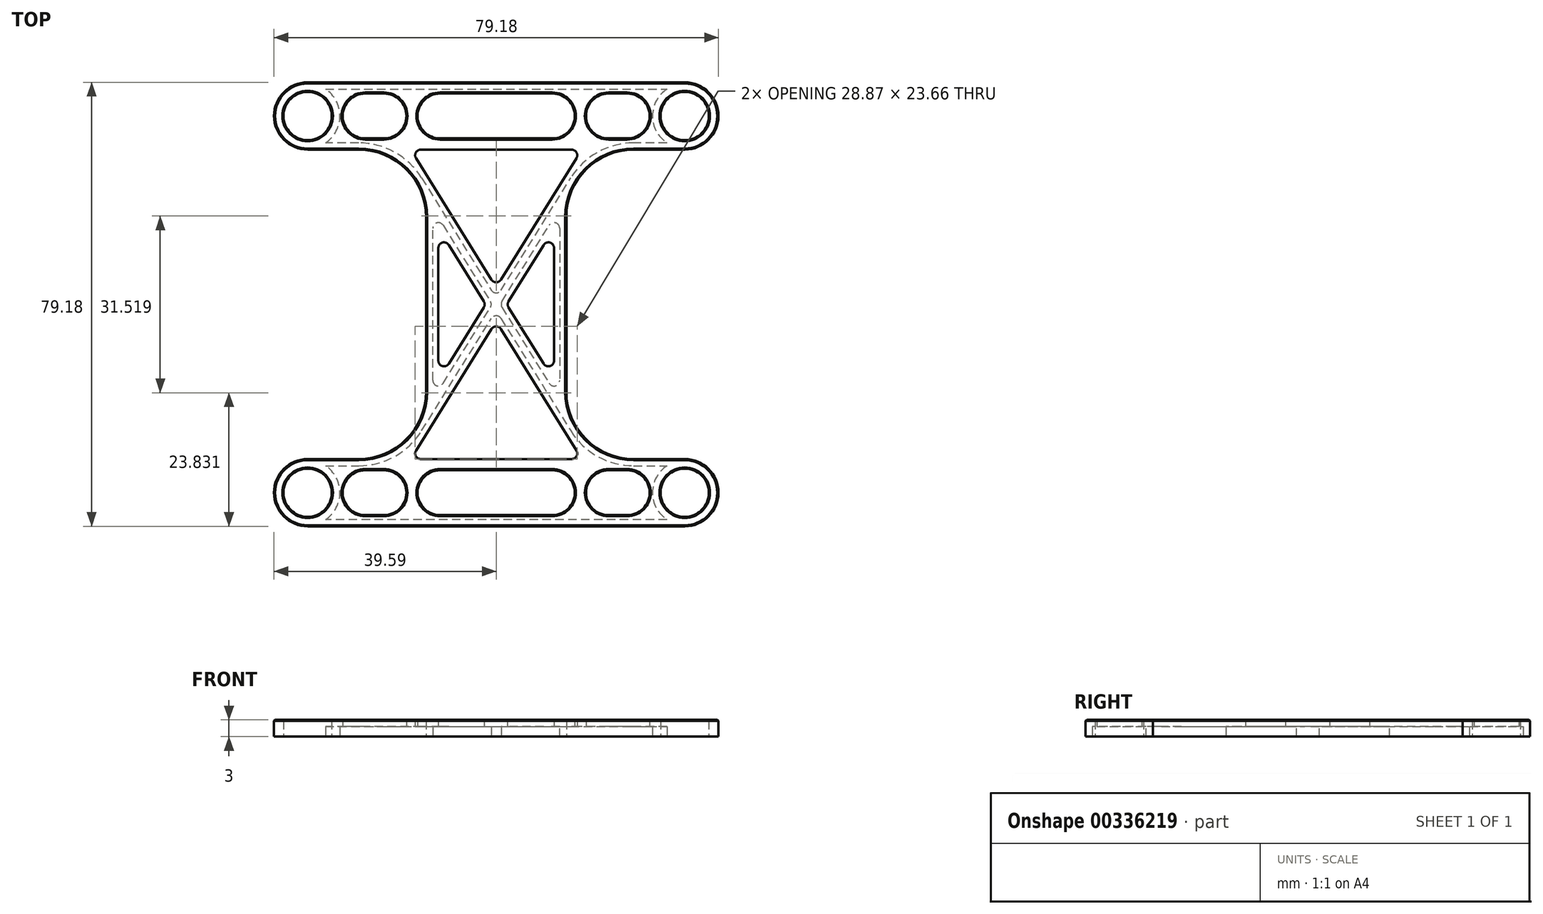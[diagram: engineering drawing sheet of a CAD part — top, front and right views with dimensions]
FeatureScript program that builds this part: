
annotation { "Feature Type Name" : "Feature", "Feature Type Description" : "" }
export const myFeature = defineFeature(function(context is Context, id is Id, definition is map)
    precondition{}
    {
        {
            var Q0;
            Q0=qCreatedBy(makeId("Top.planeOp"),FACE);
            var sketch = newSketch(context, id + "F0", { "sketchPlane" : qUnion([Q0])});
            skLineSegment(sketch, "E0.bottom", {"start": v(33.59, 33.59) * mm, "end": v(-33.59, 33.59) * mm, "construction": true});
            skLineSegment(sketch, "E0.top", {"start": v(33.59, -33.59) * mm, "end": v(-33.59, -33.59) * mm, "construction": true});
            skLineSegment(sketch, "E0.left", {"start": v(33.59, 33.59) * mm, "end": v(33.59, -33.59) * mm, "construction": true});
            skLineSegment(sketch, "E0.right", {"start": v(-33.59, 33.59) * mm, "end": v(-33.59, -33.59) * mm, "construction": true});
            skPoint(sketch, "E0.middle", {"position": v(0, 0) * mm});
            skCircle(sketch, "E1", {"center": v(33.59, 33.59) * mm, "radius": 4.25 * mm, "construction": true});
            skCircle(sketch, "E2", {"center": v(-33.59, 33.59) * mm, "radius": 4.25 * mm, "construction": true});
            skCircle(sketch, "E3", {"center": v(-33.59, -33.59) * mm, "radius": 4.25 * mm, "construction": true});
            skCircle(sketch, "E4", {"center": v(33.59, -33.59) * mm, "radius": 4.25 * mm, "construction": true});
            skLineSegment(sketch, "E5.bottom", {"start": v(10, 16.5) * mm, "end": v(-10, 16.5) * mm, "construction": true});
            skLineSegment(sketch, "E5.top", {"start": v(10, -16.5) * mm, "end": v(-10, -16.5) * mm, "construction": true});
            skLineSegment(sketch, "E5.left", {"start": v(10, 16.5) * mm, "end": v(10, -16.5) * mm, "construction": true});
            skLineSegment(sketch, "E5.right", {"start": v(-10, 16.5) * mm, "end": v(-10, -16.5) * mm, "construction": true});
            skLineSegment(sketch, "E6", {"start": v(33.59, 33.59) * mm, "end": v(-33.59, -33.59) * mm, "construction": true});
            skSolve(sketch);
        }
        {
            var Q0;
            Q0=qCreatedBy(makeId("Top.planeOp"),FACE);
            var sketch = newSketch(context, id + "F1", { "sketchPlane" : qUnion([Q0])});
            skCircle(sketch, "E7.0", {"center": v(33.59, 33.59) * mm, "radius": 4.25 * mm, "construction": true});
            skCircle(sketch, "E8.0", {"center": v(-33.59, 33.59) * mm, "radius": 4.25 * mm, "construction": true});
            skCircle(sketch, "E9.0", {"center": v(-33.59, -33.59) * mm, "radius": 4.25 * mm, "construction": true});
            skCircle(sketch, "E10.0", {"center": v(33.59, -33.59) * mm, "radius": 4.25 * mm, "construction": true});
            skLineSegment(sketch, "E11.0", {"start": v(33.59, 33.59) * mm, "end": v(33.59, -33.59) * mm, "construction": true});
            skLineSegment(sketch, "E12.0", {"start": v(33.59, 33.59) * mm, "end": v(-33.59, 33.59) * mm, "construction": true});
            skLineSegment(sketch, "E13.0", {"start": v(-33.59, 33.59) * mm, "end": v(-33.59, -33.59) * mm, "construction": true});
            skLineSegment(sketch, "E14.0", {"start": v(33.59, -33.59) * mm, "end": v(-33.59, -33.59) * mm, "construction": true});
            skArc(sketch, "E15.0.startCap", {"start": v(33.59, 39.59) * mm, "mid": v(39.59, 33.59) * mm, "end": v(33.59, 27.59) * mm});
            skArc(sketch, "E15.0.endCap", {"start": v(-33.59, 27.59) * mm, "mid": v(-39.59, 33.59) * mm, "end": v(-33.59, 39.59) * mm});
            skLineSegment(sketch, "E15.0.left", {"start": v(33.59, 27.59) * mm, "end": v(24.5, 27.59) * mm});
            skLineSegment(sketch, "E15.0.right", {"start": v(33.59, 39.59) * mm, "end": v(-33.59, 39.59) * mm});
            skArc(sketch, "E16.0.startCap", {"start": v(33.59, -27.59) * mm, "mid": v(39.59, -33.59) * mm, "end": v(33.59, -39.59) * mm});
            skArc(sketch, "E16.0.endCap", {"start": v(-33.59, -39.59) * mm, "mid": v(-39.59, -33.59) * mm, "end": v(-33.59, -27.59) * mm});
            skLineSegment(sketch, "E16.0.left", {"start": v(33.59, -39.59) * mm, "end": v(-33.59, -39.59) * mm});
            skLineSegment(sketch, "E16.0.right", {"start": v(33.59, -27.59) * mm, "end": v(24.5, -27.59) * mm});
            skLineSegment(sketch, "E17", {"start": v(-12.5, 15.59) * mm, "end": v(-12.5, -15.59) * mm});
            skLineSegment(sketch, "E18", {"start": v(12.5, 15.59) * mm, "end": v(12.5, -15.59) * mm});
            skLineSegment(sketch, "E19.trimOffspring", {"start": v(-24.5, 27.59) * mm, "end": v(-33.59, 27.59) * mm});
            skLineSegment(sketch, "E20.trimOffspring", {"start": v(-24.5, -27.59) * mm, "end": v(-33.59, -27.59) * mm});
            skPoint(sketch, "E21.visualSharp", {"position": v(12.5, 27.59) * mm});
            skArc(sketch, "E21.filletArc", {"start": v(24.5, 27.59) * mm, "mid": v(16.01, 24.07) * mm, "end": v(12.5, 15.59) * mm});
            skPoint(sketch, "E22.visualSharp", {"position": v(-12.5, 27.59) * mm});
            skArc(sketch, "E22.filletArc", {"start": v(-12.5, 15.59) * mm, "mid": v(-16.01, 24.07) * mm, "end": v(-24.5, 27.59) * mm});
            skPoint(sketch, "E23.visualSharp", {"position": v(-12.5, -27.59) * mm});
            skArc(sketch, "E23.filletArc", {"start": v(-24.5, -27.59) * mm, "mid": v(-16.01, -24.07) * mm, "end": v(-12.5, -15.59) * mm});
            skPoint(sketch, "E24.visualSharp", {"position": v(12.5, -27.59) * mm});
            skArc(sketch, "E24.filletArc", {"start": v(12.5, -15.59) * mm, "mid": v(16.01, -24.07) * mm, "end": v(24.5, -27.59) * mm});
            skSolve(sketch);
        }
        {
            var Q0;
            Q0=qCreatedBy(makeId("Top.planeOp"),FACE);
            var sketch = newSketch(context, id + "F2", { "sketchPlane" : qUnion([Q0])});
            skCircle(sketch, "E25.0", {"center": v(-33.59, 33.59) * mm, "radius": 4.25 * mm, "construction": true});
            skCircle(sketch, "E26.0", {"center": v(33.59, 33.59) * mm, "radius": 4.25 * mm, "construction": true});
            skCircle(sketch, "E27.0", {"center": v(-33.59, -33.59) * mm, "radius": 4.25 * mm, "construction": true});
            skCircle(sketch, "E28.0", {"center": v(33.59, -33.59) * mm, "radius": 4.25 * mm, "construction": true});
            skCircle(sketch, "E29.0", {"center": v(33.59, 33.59) * mm, "radius": 4.3 * mm});
            skCircle(sketch, "E30.0", {"center": v(-33.59, -33.59) * mm, "radius": 4.3 * mm});
            skCircle(sketch, "E31.0", {"center": v(33.59, -33.59) * mm, "radius": 4.3 * mm});
            skLineSegment(sketch, "E32", {"start": v(-23.34, 33.59) * mm, "end": v(-20, 33.59) * mm});
            skLineSegment(sketch, "E33", {"start": v(-10, 33.59) * mm, "end": v(10, 33.59) * mm});
            skArc(sketch, "E34.0.startCap", {"start": v(-23.34, 29.59) * mm, "mid": v(-27.34, 33.59) * mm, "end": v(-23.34, 37.59) * mm});
            skArc(sketch, "E34.0.endCap", {"start": v(-20, 37.59) * mm, "mid": v(-16, 33.59) * mm, "end": v(-20, 29.59) * mm});
            skLineSegment(sketch, "E34.0.left", {"start": v(-23.34, 37.59) * mm, "end": v(-20, 37.59) * mm});
            skLineSegment(sketch, "E34.0.right", {"start": v(-23.34, 29.59) * mm, "end": v(-20, 29.59) * mm});
            skArc(sketch, "E35.0.startCap", {"start": v(-10, 29.59) * mm, "mid": v(-14, 33.59) * mm, "end": v(-10, 37.59) * mm});
            skArc(sketch, "E35.0.endCap", {"start": v(10, 37.59) * mm, "mid": v(14, 33.59) * mm, "end": v(10, 29.59) * mm});
            skLineSegment(sketch, "E35.0.left", {"start": v(-10, 37.59) * mm, "end": v(10, 37.59) * mm});
            skLineSegment(sketch, "E35.0.right", {"start": v(-10, 29.59) * mm, "end": v(10, 29.59) * mm});
            skLineSegment(sketch, "E36", {"start": v(-16, 33.59) * mm, "end": v(-14, 33.59) * mm, "construction": true});
            skCircle(sketch, "E37.0", {"center": v(-33.59, 33.59) * mm, "radius": 4.3 * mm});
            skLineSegment(sketch, "E38", {"start": v(-27.34, 33.59) * mm, "end": v(-29.34, 33.59) * mm, "construction": true});
            skArc(sketch, "E39.MirrorCS", {"start": v(23.34, 29.59) * mm, "mid": v(27.34, 33.59) * mm, "end": v(23.34, 37.59) * mm});
            skLineSegment(sketch, "E40.MirrorCS", {"start": v(23.34, 37.59) * mm, "end": v(20, 37.59) * mm});
            skArc(sketch, "E41.MirrorCS", {"start": v(20, 37.59) * mm, "mid": v(16, 33.59) * mm, "end": v(20, 29.59) * mm});
            skLineSegment(sketch, "E42.MirrorCS", {"start": v(23.34, 29.59) * mm, "end": v(20, 29.59) * mm});
            skArc(sketch, "E43.MirrorCS", {"start": v(-23.34, -29.59) * mm, "mid": v(-27.34, -33.59) * mm, "end": v(-23.34, -37.59) * mm});
            skLineSegment(sketch, "E44.MirrorCS", {"start": v(-23.34, -37.59) * mm, "end": v(-20, -37.59) * mm});
            skLineSegment(sketch, "E45.MirrorCS", {"start": v(-23.34, -29.59) * mm, "end": v(-20, -29.59) * mm});
            skArc(sketch, "E46.MirrorCS", {"start": v(-20, -37.59) * mm, "mid": v(-16, -33.59) * mm, "end": v(-20, -29.59) * mm});
            skArc(sketch, "E47.MirrorCS", {"start": v(-10, -29.59) * mm, "mid": v(-14, -33.59) * mm, "end": v(-10, -37.59) * mm});
            skLineSegment(sketch, "E48.MirrorCS", {"start": v(-10, -29.59) * mm, "end": v(10, -29.59) * mm});
            skLineSegment(sketch, "E49.MirrorCS", {"start": v(-10, -37.59) * mm, "end": v(10, -37.59) * mm});
            skArc(sketch, "E50.MirrorCS", {"start": v(10, -37.59) * mm, "mid": v(14, -33.59) * mm, "end": v(10, -29.59) * mm});
            skArc(sketch, "E51.MirrorCS", {"start": v(20, -37.59) * mm, "mid": v(16, -33.59) * mm, "end": v(20, -29.59) * mm});
            skLineSegment(sketch, "E52.MirrorCS", {"start": v(23.34, -37.59) * mm, "end": v(20, -37.59) * mm});
            skLineSegment(sketch, "E53.MirrorCS", {"start": v(23.34, -29.59) * mm, "end": v(20, -29.59) * mm});
            skArc(sketch, "E54.MirrorCS", {"start": v(23.34, -29.59) * mm, "mid": v(27.34, -33.59) * mm, "end": v(23.34, -37.59) * mm});
            skSolve(sketch);
        }
        {
            var Q0;
            Q0=qCreatedBy(makeId("Top.planeOp"),FACE);
            var sketch = newSketch(context, id + "F3", { "sketchPlane" : qUnion([Q0])});
            skPoint(sketch, "E55.0", {"position": v(-33.59, 33.59) * mm});
            skPoint(sketch, "E56.0", {"position": v(33.59, 33.59) * mm});
            skPoint(sketch, "E57.0", {"position": v(33.59, -33.59) * mm});
            skPoint(sketch, "E58.0", {"position": v(-33.59, -33.59) * mm});
            skCircle(sketch, "E59.0", {"center": v(-33.59, 33.59) * mm, "radius": 4.25 * mm, "construction": true});
            skCircle(sketch, "E60.0", {"center": v(33.59, 33.59) * mm, "radius": 4.25 * mm, "construction": true});
            skCircle(sketch, "E61.0", {"center": v(33.59, -33.59) * mm, "radius": 4.25 * mm, "construction": true});
            skCircle(sketch, "E62.0", {"center": v(-33.59, -33.59) * mm, "radius": 4.25 * mm, "construction": true});
            skCircle(sketch, "E63.0", {"center": v(33.59, 33.59) * mm, "radius": 5.75 * mm});
            skCircle(sketch, "E64.0", {"center": v(-33.59, 33.59) * mm, "radius": 5.75 * mm});
            skCircle(sketch, "E65.0", {"center": v(33.59, -33.59) * mm, "radius": 5.75 * mm});
            skCircle(sketch, "E66.0", {"center": v(-33.59, -33.59) * mm, "radius": 5.75 * mm});
            skSolve(sketch);
        }
        {
            var Q0;
            Q0=qCreatedBy(makeId("Front.planeOp"),FACE);
            var sketch = newSketch(context, id + "F4", { "sketchPlane" : qUnion([Q0])});
            skLineSegment(sketch, "E67", {"start": v(0, 0) * mm, "end": v(0, -3) * mm});
            skLineSegment(sketch, "E68", {"start": v(0, -3) * mm, "end": v(0, -6) * mm});
            skSolve(sketch);
        }
        {
            var Q0;
            Q0=qSketchRegion(id+"F1",true);
            var Q1;
            Q1=sQuery(id+"F4.wireOp",EDGE,"E67");
            sweep(context, id + "F5", {"profiles" : qUnion([Q0]), "path" : qUnion([Q1])});
        }
        {
            var Q0;
            Q0=makeQuery(id+"F5.opSweep","CAP_FACE",FACE,{"disambiguationData":[OSD([sQuery(id+"F1.wireOp",EDGE,"E15.0.startCap"),sQuery(id+"F1.wireOp",EDGE,"E15.0.endCap"),sQuery(id+"F1.wireOp",EDGE,"E15.0.left"),sQuery(id+"F1.wireOp",EDGE,"E15.0.right"),sQuery(id+"F1.wireOp",EDGE,"E16.0.startCap"),sQuery(id+"F1.wireOp",EDGE,"E16.0.endCap"),sQuery(id+"F1.wireOp",EDGE,"E16.0.left"),sQuery(id+"F1.wireOp",EDGE,"E16.0.right"),sQuery(id+"F1.wireOp",EDGE,"E17"),sQuery(id+"F1.wireOp",EDGE,"E18"),sQuery(id+"F1.wireOp",EDGE,"E19.trimOffspring"),sQuery(id+"F1.wireOp",EDGE,"E20.trimOffspring"),sQuery(id+"F1.wireOp",EDGE,"E21.filletArc"),sQuery(id+"F1.wireOp",EDGE,"E22.filletArc"),sQuery(id+"F1.wireOp",EDGE,"E23.filletArc"),sQuery(id+"F1.wireOp",EDGE,"E24.filletArc"),sQuery(id+"F4.wireOp",VERTEX,"E67.end")])],"isStart":false});
            shell(context, id + "F6", {"entities" : qUnion([Q0]), "thickness" : 1.2 * mm});
        }
        {
            var Q0;
            Q0=qSketchRegion(id+"F3",true);
            var Q1;
            Q1=sQuery(id+"F4.wireOp",EDGE,"E67");
            sweep(context, id + "F7", {"operationType" : NewBodyOperationType.ADD, "profiles" : qUnion([Q0]), "path" : qUnion([Q1])});
        }
        {
            var Q0;
            Q0=qSketchRegion(id+"F2",true);
            var Q1;
            Q1=sQuery(id+"F4.wireOp",EDGE,"E67");
            var Q2;
            Q2=sQuery(id+"F4.wireOp",EDGE,"E68");
            sweep(context, id + "F8", {"operationType" : NewBodyOperationType.REMOVE, "profiles" : qUnion([Q0]), "path" : qUnion([Q1, Q2])});
        }
        {
            var Q0;
            Q0=makeQuery(id+"F5.opSweep","CAP_FACE",FACE,{"disambiguationData":[OSD([sQuery(id+"F1.wireOp",EDGE,"E15.0.startCap"),sQuery(id+"F1.wireOp",EDGE,"E15.0.endCap"),sQuery(id+"F1.wireOp",EDGE,"E15.0.left"),sQuery(id+"F1.wireOp",EDGE,"E15.0.right"),sQuery(id+"F1.wireOp",EDGE,"E16.0.startCap"),sQuery(id+"F1.wireOp",EDGE,"E16.0.endCap"),sQuery(id+"F1.wireOp",EDGE,"E16.0.left"),sQuery(id+"F1.wireOp",EDGE,"E16.0.right"),sQuery(id+"F1.wireOp",EDGE,"E17"),sQuery(id+"F1.wireOp",EDGE,"E18"),sQuery(id+"F1.wireOp",EDGE,"E19.trimOffspring"),sQuery(id+"F1.wireOp",EDGE,"E20.trimOffspring"),sQuery(id+"F1.wireOp",EDGE,"E21.filletArc"),sQuery(id+"F1.wireOp",EDGE,"E22.filletArc"),sQuery(id+"F1.wireOp",EDGE,"E23.filletArc"),sQuery(id+"F1.wireOp",EDGE,"E24.filletArc"),sQuery(id+"F4.wireOp",VERTEX,"E67.start")])],"isStart":true});
            chamfer(context, id + "F9", {"entities" : qUnion([Q0]), "width" : 0.2 * mm});
        }
        {
            var Q0;
            {var subQ0=sQuery(id+"F4.wireOp",VERTEX,"E67.end");Q0=makeQuery(id+"F7.boolean.opBoolean","MERGE",FACE,{"derivedFrom":[makeQuery(id+"F5.opSweep","CAP_FACE",FACE,{"disambiguationData":[OSD([sQuery(id+"F1.wireOp",EDGE,"E15.0.startCap"),sQuery(id+"F1.wireOp",EDGE,"E15.0.endCap"),sQuery(id+"F1.wireOp",EDGE,"E15.0.left"),sQuery(id+"F1.wireOp",EDGE,"E15.0.right"),sQuery(id+"F1.wireOp",EDGE,"E16.0.startCap"),sQuery(id+"F1.wireOp",EDGE,"E16.0.endCap"),sQuery(id+"F1.wireOp",EDGE,"E16.0.left"),sQuery(id+"F1.wireOp",EDGE,"E16.0.right"),sQuery(id+"F1.wireOp",EDGE,"E17"),sQuery(id+"F1.wireOp",EDGE,"E18"),sQuery(id+"F1.wireOp",EDGE,"E19.trimOffspring"),sQuery(id+"F1.wireOp",EDGE,"E20.trimOffspring"),sQuery(id+"F1.wireOp",EDGE,"E21.filletArc"),sQuery(id+"F1.wireOp",EDGE,"E22.filletArc"),sQuery(id+"F1.wireOp",EDGE,"E23.filletArc"),sQuery(id+"F1.wireOp",EDGE,"E24.filletArc"),subQ0])],"isStart":false}),makeQuery(id+"F7.opSweep","CAP_FACE",FACE,{"disambiguationData":[OSD([sQuery(id+"F3.wireOp",EDGE,"E63.0"),subQ0])],"isStart":false}),makeQuery(id+"F7.opSweep","CAP_FACE",FACE,{"disambiguationData":[OSD([sQuery(id+"F3.wireOp",EDGE,"E64.0"),subQ0])],"isStart":false}),makeQuery(id+"F7.opSweep","CAP_FACE",FACE,{"disambiguationData":[OSD([sQuery(id+"F3.wireOp",EDGE,"E65.0"),subQ0])],"isStart":false}),makeQuery(id+"F7.opSweep","CAP_FACE",FACE,{"disambiguationData":[OSD([sQuery(id+"F3.wireOp",EDGE,"E66.0"),subQ0])],"isStart":false})]});}
            var sketch = newSketch(context, id + "F10", { "sketchPlane" : qUnion([Q0])});
            skLineSegment(sketch, "E69", {"start": v(-13.28, -22.55) * mm, "end": v(14.3, 21.91) * mm});
            skLineSegment(sketch, "E70", {"start": v(-13.28, 22.55) * mm, "end": v(14.3, -21.91) * mm});
            skLineSegment(sketch, "E71", {"start": v(-14.3, -21.91) * mm, "end": v(13.28, 22.55) * mm});
            skLineSegment(sketch, "E72", {"start": v(-14.3, 21.91) * mm, "end": v(13.28, -22.55) * mm});
            skLineSegment(sketch, "E73", {"start": v(-14.3, -21.91) * mm, "end": v(-13.28, -22.55) * mm});
            skLineSegment(sketch, "E74", {"start": v(13.28, -22.55) * mm, "end": v(14.3, -21.91) * mm});
            skLineSegment(sketch, "E75", {"start": v(13.28, 22.55) * mm, "end": v(14.3, 21.91) * mm});
            skLineSegment(sketch, "E76", {"start": v(-13.28, 22.55) * mm, "end": v(-14.3, 21.91) * mm});
            skSolve(sketch);
        }
        {
            var Q0;
            Q0 = qSketchRegion(id + "F10", true);
            var Q1;
            Q1=makeQuery(id+"F6.opShell","OFFSET_FACE",FACE,{"disambiguationData":[OSD([sQuery(id+"F1.wireOp",EDGE,"E15.0.startCap"),sQuery(id+"F1.wireOp",EDGE,"E15.0.endCap"),sQuery(id+"F1.wireOp",EDGE,"E15.0.left"),sQuery(id+"F1.wireOp",EDGE,"E15.0.right"),sQuery(id+"F1.wireOp",EDGE,"E16.0.startCap"),sQuery(id+"F1.wireOp",EDGE,"E16.0.endCap"),sQuery(id+"F1.wireOp",EDGE,"E16.0.left"),sQuery(id+"F1.wireOp",EDGE,"E16.0.right"),sQuery(id+"F1.wireOp",EDGE,"E17"),sQuery(id+"F1.wireOp",EDGE,"E18"),sQuery(id+"F1.wireOp",EDGE,"E19.trimOffspring"),sQuery(id+"F1.wireOp",EDGE,"E20.trimOffspring"),sQuery(id+"F1.wireOp",EDGE,"E21.filletArc"),sQuery(id+"F1.wireOp",EDGE,"E22.filletArc"),sQuery(id+"F1.wireOp",EDGE,"E23.filletArc"),sQuery(id+"F1.wireOp",EDGE,"E24.filletArc"),sQuery(id+"F4.wireOp",VERTEX,"E67.start")])]});
            extrude(context, id + "F11", {"entities" : qUnion([Q0]), "operationType" : NewBodyOperationType.ADD, "endBound" : BoundingType.UP_TO_SURFACE, "oppositeDirection" : true, "endBoundEntityFace" : qUnion([Q1]), "depth" : 25 * mm});
        }
        {
            var Q0;
            Q0=makeQuery(id+"F11.opExtrude","SWEPT_EDGE",EDGE,{"disambiguationData":[OSD([sQuery(id+"F10.wireOp",EDGE,"E69"),sQuery(id+"F10.wireOp",EDGE,"E72")])]});
            var Q1;
            Q1=makeQuery(id+"F11.opExtrude","SWEPT_EDGE",EDGE,{"disambiguationData":[OSD([sQuery(id+"F10.wireOp",EDGE,"E69"),sQuery(id+"F10.wireOp",EDGE,"E70")])]});
            var Q2;
            Q2=makeQuery(id+"F11.opExtrude","SWEPT_EDGE",EDGE,{"disambiguationData":[OSD([sQuery(id+"F10.wireOp",EDGE,"E71"),sQuery(id+"F10.wireOp",EDGE,"E72")])]});
            var Q3;
            Q3=makeQuery(id+"F11.opExtrude","SWEPT_EDGE",EDGE,{"disambiguationData":[OSD([sQuery(id+"F10.wireOp",EDGE,"E70"),sQuery(id+"F10.wireOp",EDGE,"E71")])]});
            var Q4;
            {var subQ0=sQuery(id+"F10.wireOp",EDGE,"E69");var subQ1=sQuery(id+"F4.wireOp",VERTEX,"E67.end");var subQ2=sQuery(id+"F1.wireOp",EDGE,"E24.filletArc");var subQ3=makeQuery(id+"F10.imprint","INTERSECT",VERTEX,{"derivedFrom":[makeQuery(id+"F6.opShell","OFFSET_EDGE",EDGE,{"disambiguationData":[OSD([subQ2,subQ1])]}),subQ0]});Q4=makeQuery(id+"F11.boolean.opBoolean","INTERSECT",EDGE,{"derivedFrom":[makeQuery(id+"F6.opShell","OFFSET_FACE",FACE,{"disambiguationData":[OSD([subQ2,sQuery(id+"F4.wireOp",EDGE,"E67")])]}),makeQuery(id+"F11.opExtrude","SWEPT_FACE",FACE,{"disambiguationData":[OSD([subQ0]),TDD([makeQuery(id+"F10.imprint","IMPRINT",EDGE,{"disambiguationData":[TD([[makeQuery(id+"F10.imprint","INTERSECT",VERTEX,{"derivedFrom":[subQ0,sQuery(id+"F10.wireOp",EDGE,"E70")]}),-1.0]])],"derivedFrom":subQ0}),makeQuery(id+"F10.imprint","IMPRINT",EDGE,{"disambiguationData":[TD([[subQ3,-1.0]])],"derivedFrom":subQ0})])]})]});}
            var Q5;
            {var subQ0=sQuery(id+"F10.wireOp",EDGE,"E72");var subQ1=sQuery(id+"F4.wireOp",VERTEX,"E67.end");var subQ2=sQuery(id+"F1.wireOp",EDGE,"E23.filletArc");var subQ3=makeQuery(id+"F10.imprint","INTERSECT",VERTEX,{"derivedFrom":[makeQuery(id+"F6.opShell","OFFSET_EDGE",EDGE,{"disambiguationData":[OSD([subQ2,subQ1])]}),subQ0]});Q5=makeQuery(id+"F11.boolean.opBoolean","INTERSECT",EDGE,{"derivedFrom":[makeQuery(id+"F6.opShell","OFFSET_FACE",FACE,{"disambiguationData":[OSD([subQ2,sQuery(id+"F4.wireOp",EDGE,"E67")])]}),makeQuery(id+"F11.opExtrude","SWEPT_FACE",FACE,{"disambiguationData":[OSD([subQ0]),TDD([makeQuery(id+"F10.imprint","IMPRINT",EDGE,{"disambiguationData":[TD([[subQ3,1.0]])],"derivedFrom":subQ0}),makeQuery(id+"F10.imprint","IMPRINT",EDGE,{"disambiguationData":[TD([[makeQuery(id+"F10.imprint","INTERSECT",VERTEX,{"derivedFrom":[sQuery(id+"F10.wireOp",EDGE,"E71"),subQ0]}),1.0]])],"derivedFrom":subQ0})])]})]});}
            var Q6;
            {var subQ0=sQuery(id+"F10.wireOp",EDGE,"E70");var subQ1=sQuery(id+"F4.wireOp",VERTEX,"E67.end");var subQ2=sQuery(id+"F1.wireOp",EDGE,"E21.filletArc");var subQ3=makeQuery(id+"F10.imprint","INTERSECT",VERTEX,{"derivedFrom":[makeQuery(id+"F6.opShell","OFFSET_EDGE",EDGE,{"disambiguationData":[OSD([subQ2,subQ1])]}),subQ0]});Q6=makeQuery(id+"F11.boolean.opBoolean","INTERSECT",EDGE,{"derivedFrom":[makeQuery(id+"F6.opShell","OFFSET_FACE",FACE,{"disambiguationData":[OSD([subQ2,sQuery(id+"F4.wireOp",EDGE,"E67")])]}),makeQuery(id+"F11.opExtrude","SWEPT_FACE",FACE,{"disambiguationData":[OSD([subQ0]),TDD([makeQuery(id+"F10.imprint","IMPRINT",EDGE,{"disambiguationData":[TD([[makeQuery(id+"F10.imprint","INTERSECT",VERTEX,{"derivedFrom":[sQuery(id+"F10.wireOp",EDGE,"E69"),subQ0]}),-1.0]])],"derivedFrom":subQ0}),makeQuery(id+"F10.imprint","IMPRINT",EDGE,{"disambiguationData":[TD([[subQ3,-1.0]])],"derivedFrom":subQ0})])]})]});}
            var Q7;
            {var subQ0=sQuery(id+"F10.wireOp",EDGE,"E71");var subQ1=sQuery(id+"F4.wireOp",VERTEX,"E67.end");var subQ2=sQuery(id+"F1.wireOp",EDGE,"E22.filletArc");var subQ3=makeQuery(id+"F10.imprint","INTERSECT",VERTEX,{"derivedFrom":[makeQuery(id+"F6.opShell","OFFSET_EDGE",EDGE,{"disambiguationData":[OSD([subQ2,subQ1])]}),subQ0]});Q7=makeQuery(id+"F11.boolean.opBoolean","INTERSECT",EDGE,{"derivedFrom":[makeQuery(id+"F6.opShell","OFFSET_FACE",FACE,{"disambiguationData":[OSD([subQ2,sQuery(id+"F4.wireOp",EDGE,"E67")])]}),makeQuery(id+"F11.opExtrude","SWEPT_FACE",FACE,{"disambiguationData":[OSD([subQ0]),TDD([makeQuery(id+"F10.imprint","IMPRINT",EDGE,{"disambiguationData":[TD([[subQ3,1.0]])],"derivedFrom":subQ0}),makeQuery(id+"F10.imprint","IMPRINT",EDGE,{"disambiguationData":[TD([[makeQuery(id+"F10.imprint","INTERSECT",VERTEX,{"derivedFrom":[subQ0,sQuery(id+"F10.wireOp",EDGE,"E72")]}),1.0]])],"derivedFrom":subQ0})])]})]});}
            fillet(context, id + "F12", {"entities" : qUnion([Q0, Q1, Q2, Q3, Q4, Q5, Q6, Q7]), "radius" : 1 * mm, "allowEdgeOverflow" : false});
        }
        {
            var Q0;
            {var subQ0=sQuery(id+"F4.wireOp",EDGE,"E67");var subQ1=sQuery(id+"F1.wireOp",EDGE,"E16.0.left");var subQ4=sQuery(id+"F1.wireOp",EDGE,"E23.filletArc");var subQ7=sQuery(id+"F1.wireOp",EDGE,"E24.filletArc");var subQ8=sQuery(id+"F1.wireOp",EDGE,"E16.0.right");var subQ9=sQuery(id+"F1.wireOp",EDGE,"E20.trimOffspring");Q0=makeQuery(id+"F11.boolean.opBoolean","SPLIT",FACE,{"disambiguationData":[TD([makeQuery(id+"F6.opShell","OFFSET_FACE",FACE,{"disambiguationData":[OSD([subQ1,subQ0])]})])],"derivedFrom":makeQuery(id+"F6.opShell","OFFSET_FACE",FACE,{"disambiguationData":[OSD([sQuery(id+"F1.wireOp",EDGE,"E15.0.startCap"),sQuery(id+"F1.wireOp",EDGE,"E15.0.endCap"),sQuery(id+"F1.wireOp",EDGE,"E15.0.left"),sQuery(id+"F1.wireOp",EDGE,"E15.0.right"),sQuery(id+"F1.wireOp",EDGE,"E16.0.startCap"),sQuery(id+"F1.wireOp",EDGE,"E16.0.endCap"),subQ1,subQ8,sQuery(id+"F1.wireOp",EDGE,"E17"),sQuery(id+"F1.wireOp",EDGE,"E18"),sQuery(id+"F1.wireOp",EDGE,"E19.trimOffspring"),subQ9,sQuery(id+"F1.wireOp",EDGE,"E21.filletArc"),sQuery(id+"F1.wireOp",EDGE,"E22.filletArc"),subQ4,subQ7,sQuery(id+"F4.wireOp",VERTEX,"E67.start")])]})});}
            var sketch = newSketch(context, id + "F13", { "sketchPlane" : qUnion([Q0])});
            skLineSegment(sketch, "E77", {"start": v(0, 29.59) * mm, "end": v(0, 28.59) * mm, "construction": true});
            skPoint(sketch, "E77.endSnap0", {"position": v(0, 29.59) * mm});
            skLineSegment(sketch, "E78.0.0", {"start": v(-13.28, 22.55) * mm, "end": v(-0.85, 2.5) * mm, "construction": true});
            skArc(sketch, "E78.0.1", {"start": v(-0.85, 2.5) * mm, "mid": v(0, 2.03) * mm, "end": v(0.85, 2.5) * mm, "construction": true});
            skLineSegment(sketch, "E78.0.2", {"start": v(0.85, 2.5) * mm, "end": v(13.28, 22.55) * mm, "construction": true});
            skArc(sketch, "E78.0.3", {"start": v(13.28, 22.55) * mm, "mid": v(17.1, 26.52) * mm, "end": v(22.21, 28.59) * mm, "construction": true});
            skLineSegment(sketch, "E78.0.4", {"start": v(24.5, 28.79) * mm, "end": v(30.42, 28.79) * mm, "construction": true});
            skArc(sketch, "E78.0.5", {"start": v(30.42, 28.79) * mm, "mid": v(27.84, 33.59) * mm, "end": v(30.42, 38.39) * mm, "construction": true});
            skLineSegment(sketch, "E78.0.6", {"start": v(30.42, 38.39) * mm, "end": v(-30.42, 38.39) * mm, "construction": true});
            skArc(sketch, "E78.0.7", {"start": v(-30.42, 38.39) * mm, "mid": v(-27.84, 33.59) * mm, "end": v(-30.42, 28.79) * mm, "construction": true});
            skLineSegment(sketch, "E78.0.8", {"start": v(-30.42, 28.79) * mm, "end": v(-24.5, 28.79) * mm, "construction": true});
            skArc(sketch, "E78.0.9", {"start": v(-24.5, 28.79) * mm, "mid": v(-23.35, 28.74) * mm, "end": v(-22.21, 28.59) * mm, "construction": true});
            skLineSegment(sketch, "E79", {"start": v(-26.79, 28.59) * mm, "end": v(26.79, 28.59) * mm, "construction": true});
            skArc(sketch, "E80", {"start": v(-22.21, 28.59) * mm, "mid": v(-17.1, 26.52) * mm, "end": v(-13.28, 22.55) * mm, "construction": true});
            skArc(sketch, "E81", {"start": v(22.21, 28.59) * mm, "mid": v(23.35, 28.74) * mm, "end": v(24.5, 28.79) * mm, "construction": true});
            skLineSegment(sketch, "E82.0", {"start": v(-15.23, 27.59) * mm, "end": v(0, 3.03) * mm});
            skLineSegment(sketch, "E82.1", {"start": v(-15.23, 27.59) * mm, "end": v(15.23, 27.59) * mm});
            skLineSegment(sketch, "E82.2", {"start": v(0, 3.03) * mm, "end": v(15.23, 27.59) * mm});
            skLineSegment(sketch, "E83.0", {"start": v(-1.88, 0) * mm, "end": v(-10.3, 13.57) * mm});
            skLineSegment(sketch, "E83.1", {"start": v(-10.3, -13.57) * mm, "end": v(-1.88, 0) * mm});
            skLineSegment(sketch, "E83.2", {"start": v(-10.3, 13.57) * mm, "end": v(-10.3, -13.57) * mm});
            skLineSegment(sketch, "E84.0", {"start": v(1.88, 0) * mm, "end": v(10.3, -13.57) * mm});
            skLineSegment(sketch, "E84.1", {"start": v(10.3, 13.57) * mm, "end": v(1.88, 0) * mm});
            skLineSegment(sketch, "E84.2", {"start": v(10.3, -13.57) * mm, "end": v(10.3, 13.57) * mm});
            skLineSegment(sketch, "E85.MirrorCS", {"start": v(-15.23, -27.59) * mm, "end": v(0, -3.03) * mm});
            skLineSegment(sketch, "E86.MirrorCS", {"start": v(0, -3.03) * mm, "end": v(15.23, -27.59) * mm});
            skLineSegment(sketch, "E87.MirrorCS", {"start": v(-15.23, -27.59) * mm, "end": v(15.23, -27.59) * mm});
            skSolve(sketch);
        }
        {
            var Q0;
            Q0 = qSketchRegion(id + "F13", true);
            extrude(context, id + "F14", {"entities" : qUnion([Q0]), "operationType" : NewBodyOperationType.REMOVE, "endBound" : BoundingType.THROUGH_ALL, "oppositeDirection" : true, "depth" : 25 * mm});
        }
        {
            var Q0;
            Q0=makeQuery(id+"F14.boolean.opBoolean","COPY",EDGE,{"derivedFrom":makeQuery(id+"F14.opExtrude","SWEPT_EDGE",EDGE,{"disambiguationData":[OSD([sQuery(id+"F13.wireOp",EDGE,"E82.0"),sQuery(id+"F13.wireOp",EDGE,"E82.1")])]})});
            var Q1;
            Q1=makeQuery(id+"F14.boolean.opBoolean","COPY",EDGE,{"derivedFrom":makeQuery(id+"F14.opExtrude","SWEPT_EDGE",EDGE,{"disambiguationData":[OSD([sQuery(id+"F13.wireOp",EDGE,"E82.1"),sQuery(id+"F13.wireOp",EDGE,"E82.2")])]})});
            var Q2;
            Q2=makeQuery(id+"F14.boolean.opBoolean","COPY",EDGE,{"derivedFrom":makeQuery(id+"F14.opExtrude","SWEPT_EDGE",EDGE,{"disambiguationData":[OSD([sQuery(id+"F13.wireOp",EDGE,"E82.0"),sQuery(id+"F13.wireOp",EDGE,"E82.2")])]})});
            var Q3;
            Q3=makeQuery(id+"F14.boolean.opBoolean","COPY",EDGE,{"derivedFrom":makeQuery(id+"F14.opExtrude","SWEPT_EDGE",EDGE,{"disambiguationData":[OSD([sQuery(id+"F13.wireOp",EDGE,"E83.0"),sQuery(id+"F13.wireOp",EDGE,"E83.1")])]})});
            var Q4;
            Q4=makeQuery(id+"F14.boolean.opBoolean","COPY",EDGE,{"derivedFrom":makeQuery(id+"F14.opExtrude","SWEPT_EDGE",EDGE,{"disambiguationData":[OSD([sQuery(id+"F13.wireOp",EDGE,"E84.0"),sQuery(id+"F13.wireOp",EDGE,"E84.1")])]})});
            var Q5;
            Q5=makeQuery(id+"F14.boolean.opBoolean","COPY",EDGE,{"derivedFrom":makeQuery(id+"F14.opExtrude","SWEPT_EDGE",EDGE,{"disambiguationData":[OSD([sQuery(id+"F13.wireOp",EDGE,"E84.1"),sQuery(id+"F13.wireOp",EDGE,"E84.2")])]})});
            var Q6;
            Q6=makeQuery(id+"F14.boolean.opBoolean","COPY",EDGE,{"derivedFrom":makeQuery(id+"F14.opExtrude","SWEPT_EDGE",EDGE,{"disambiguationData":[OSD([sQuery(id+"F13.wireOp",EDGE,"E83.0"),sQuery(id+"F13.wireOp",EDGE,"E83.2")])]})});
            var Q7;
            Q7=makeQuery(id+"F14.boolean.opBoolean","COPY",EDGE,{"derivedFrom":makeQuery(id+"F14.opExtrude","SWEPT_EDGE",EDGE,{"disambiguationData":[OSD([sQuery(id+"F13.wireOp",EDGE,"E84.0"),sQuery(id+"F13.wireOp",EDGE,"E84.2")])]})});
            var Q8;
            Q8=makeQuery(id+"F14.boolean.opBoolean","COPY",EDGE,{"derivedFrom":makeQuery(id+"F14.opExtrude","SWEPT_EDGE",EDGE,{"disambiguationData":[OSD([sQuery(id+"F13.wireOp",EDGE,"E85.MirrorCS"),sQuery(id+"F13.wireOp",EDGE,"E86.MirrorCS")])]})});
            var Q9;
            Q9=makeQuery(id+"F14.boolean.opBoolean","COPY",EDGE,{"derivedFrom":makeQuery(id+"F14.opExtrude","SWEPT_EDGE",EDGE,{"disambiguationData":[OSD([sQuery(id+"F13.wireOp",EDGE,"E85.MirrorCS"),sQuery(id+"F13.wireOp",EDGE,"E87.MirrorCS")])]})});
            var Q10;
            Q10=makeQuery(id+"F14.boolean.opBoolean","COPY",EDGE,{"derivedFrom":makeQuery(id+"F14.opExtrude","SWEPT_EDGE",EDGE,{"disambiguationData":[OSD([sQuery(id+"F13.wireOp",EDGE,"E86.MirrorCS"),sQuery(id+"F13.wireOp",EDGE,"E87.MirrorCS")])]})});
            var Q11;
            Q11=makeQuery(id+"F14.boolean.opBoolean","COPY",EDGE,{"derivedFrom":makeQuery(id+"F14.opExtrude","SWEPT_EDGE",EDGE,{"disambiguationData":[OSD([sQuery(id+"F13.wireOp",EDGE,"E83.1"),sQuery(id+"F13.wireOp",EDGE,"E83.2")])]})});
            fillet(context, id + "F15", {"entities" : qUnion([Q0, Q1, Q2, Q3, Q4, Q5, Q6, Q7, Q8, Q9, Q10, Q11]), "radius" : 1 * mm, "allowEdgeOverflow" : false});
        }
    });
